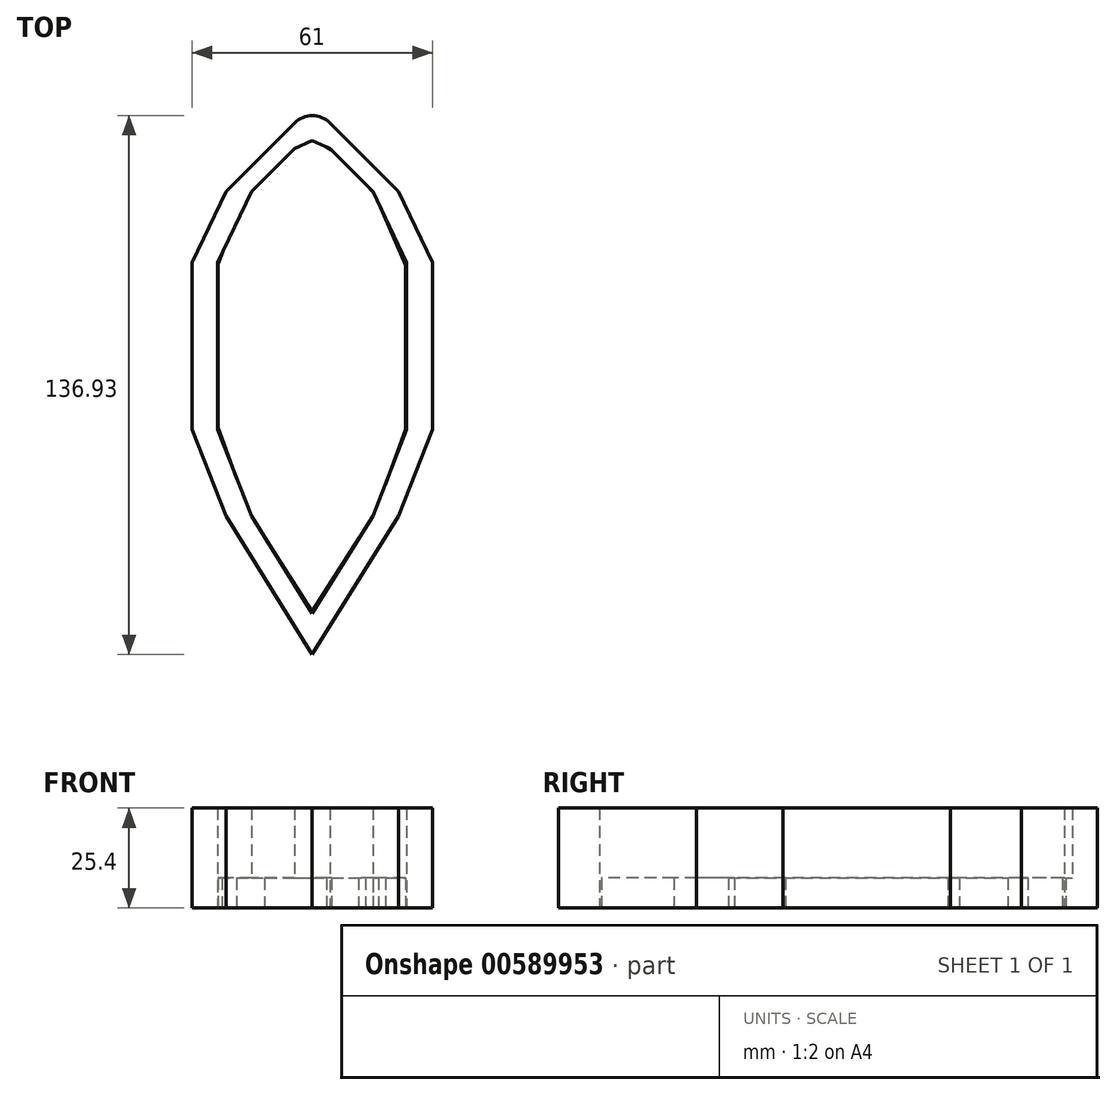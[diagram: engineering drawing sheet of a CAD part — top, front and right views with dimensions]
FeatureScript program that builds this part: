
annotation { "Feature Type Name" : "Feature", "Feature Type Description" : "" }
export const myFeature = defineFeature(function(context is Context, id is Id, definition is map)
    precondition{}
    {
        {
            var Q0;
            Q0=qCreatedBy(makeId("Top.planeOp"),FACE);
            var sketch = newSketch(context, id + "F0", { "sketchPlane" : qUnion([Q0])});
            skLineSegment(sketch, "E0", {"start": v(0, -65.2) * mm, "end": v(-21.95, -30.04) * mm});
            skLineSegment(sketch, "E1", {"start": v(-21.95, -30.04) * mm, "end": v(-30.5, -8.05) * mm});
            skLineSegment(sketch, "E2", {"start": v(-30.5, -8.05) * mm, "end": v(-30.5, 34.4) * mm});
            skLineSegment(sketch, "E3", {"start": v(-30.5, 34.4) * mm, "end": v(-21.95, 52.41) * mm});
            skLineSegment(sketch, "E4", {"start": v(-21.95, 52.41) * mm, "end": v(-4.5, 69.87) * mm});
            skLineSegment(sketch, "E5", {"start": v(4.5, 69.87) * mm, "end": v(21.95, 52.41) * mm});
            skLineSegment(sketch, "E6", {"start": v(21.95, 52.41) * mm, "end": v(30.5, 34.4) * mm});
            skLineSegment(sketch, "E7", {"start": v(30.5, 34.4) * mm, "end": v(30.5, -8.05) * mm});
            skLineSegment(sketch, "E8", {"start": v(30.5, -8.05) * mm, "end": v(21.95, -30.04) * mm});
            skLineSegment(sketch, "E9", {"start": v(21.95, -30.04) * mm, "end": v(0, -65.2) * mm});
            skPoint(sketch, "E10.visualSharp", {"position": v(0, 74.36) * mm});
            skArc(sketch, "E10.filletArc", {"start": v(4.5, 69.87) * mm, "mid": v(0, 71.73) * mm, "end": v(-4.5, 69.87) * mm});
            skLineSegment(sketch, "E11", {"start": v(-4.5, 63.37) * mm, "end": v(-15.45, 52.41) * mm});
            skLineSegment(sketch, "E12", {"start": v(-15.45, 52.41) * mm, "end": v(-24, 34.4) * mm});
            skLineSegment(sketch, "E13", {"start": v(-24, 34.4) * mm, "end": v(-24, -8.05) * mm});
            skLineSegment(sketch, "E14", {"start": v(-24, -8.05) * mm, "end": v(-15.45, -30.04) * mm});
            skLineSegment(sketch, "E15", {"start": v(-15.45, -30.04) * mm, "end": v(0, -54.78) * mm});
            skLineSegment(sketch, "E16", {"start": v(0, 65.38) * mm, "end": v(0, -72.83) * mm, "construction": true});
            skLineSegment(sketch, "E17.MirrorCS", {"start": v(4.5, 63.37) * mm, "end": v(15.45, 52.41) * mm});
            skLineSegment(sketch, "E18.MirrorCS", {"start": v(15.45, 52.41) * mm, "end": v(24, 34.4) * mm});
            skLineSegment(sketch, "E19.MirrorCS", {"start": v(24, 34.4) * mm, "end": v(24, -8.05) * mm});
            skLineSegment(sketch, "E20.MirrorCS", {"start": v(24, -8.05) * mm, "end": v(15.45, -30.04) * mm});
            skLineSegment(sketch, "E21.MirrorCS", {"start": v(15.45, -30.04) * mm, "end": v(0, -54.78) * mm});
            skLineSegment(sketch, "E22", {"start": v(-4.5, 63.37) * mm, "end": v(0, 65.38) * mm});
            skLineSegment(sketch, "E23", {"start": v(4.5, 63.37) * mm, "end": v(0, 65.38) * mm});
            skSolve(sketch);
        }
        {
            var Q0;
            Q0 = qSketchRegion(id + "F0", true);
            extrude(context, id + "F1", {"entities" : qUnion([Q0]), "depth" : 25.4 * mm, "offsetDistance" : 25.4 * mm});
        }
        {
            var Q0;
            Q0=qCreatedBy(makeId("Top.planeOp"),FACE);
            var sketch = newSketch(context, id + "F2", { "sketchPlane" : qUnion([Q0])});
            skLineSegment(sketch, "E24", {"start": v(-23.97, 34.05) * mm, "end": v(-23.97, -7.48) * mm});
            skLineSegment(sketch, "E25", {"start": v(-23.97, -7.48) * mm, "end": v(-15.73, -29.77) * mm});
            skLineSegment(sketch, "E26", {"start": v(-15.73, -29.77) * mm, "end": v(0, -54.2) * mm});
            skLineSegment(sketch, "E27", {"start": v(0, -54.2) * mm, "end": v(15.73, -29.77) * mm});
            skLineSegment(sketch, "E28", {"start": v(15.73, -29.77) * mm, "end": v(23.67, -8.1) * mm});
            skLineSegment(sketch, "E29", {"start": v(23.67, -8.1) * mm, "end": v(23.67, 33.74) * mm});
            skLineSegment(sketch, "E30", {"start": v(23.67, 33.74) * mm, "end": v(15.73, 52.07) * mm});
            skLineSegment(sketch, "E31", {"start": v(15.73, 52.07) * mm, "end": v(5.65, 62.45) * mm});
            skLineSegment(sketch, "E32", {"start": v(5.65, 62.45) * mm, "end": v(0, 66.12) * mm});
            skLineSegment(sketch, "E33", {"start": v(0, 66.12) * mm, "end": v(-6.57, 62.45) * mm});
            skLineSegment(sketch, "E34", {"start": v(-6.57, 62.45) * mm, "end": v(-16.17, 53.13) * mm});
            skLineSegment(sketch, "E35", {"start": v(-16.17, 53.13) * mm, "end": v(-23.97, 34.05) * mm});
            skSolve(sketch);
        }
        {
            var Q0;
            Q0 = qSketchRegion(id + "F2", true);
            extrude(context, id + "F3", {"entities" : qUnion([Q0]), "operationType" : NewBodyOperationType.ADD, "depth" : 7.62 * mm, "offsetDistance" : 25.4 * mm});
        }
    });
